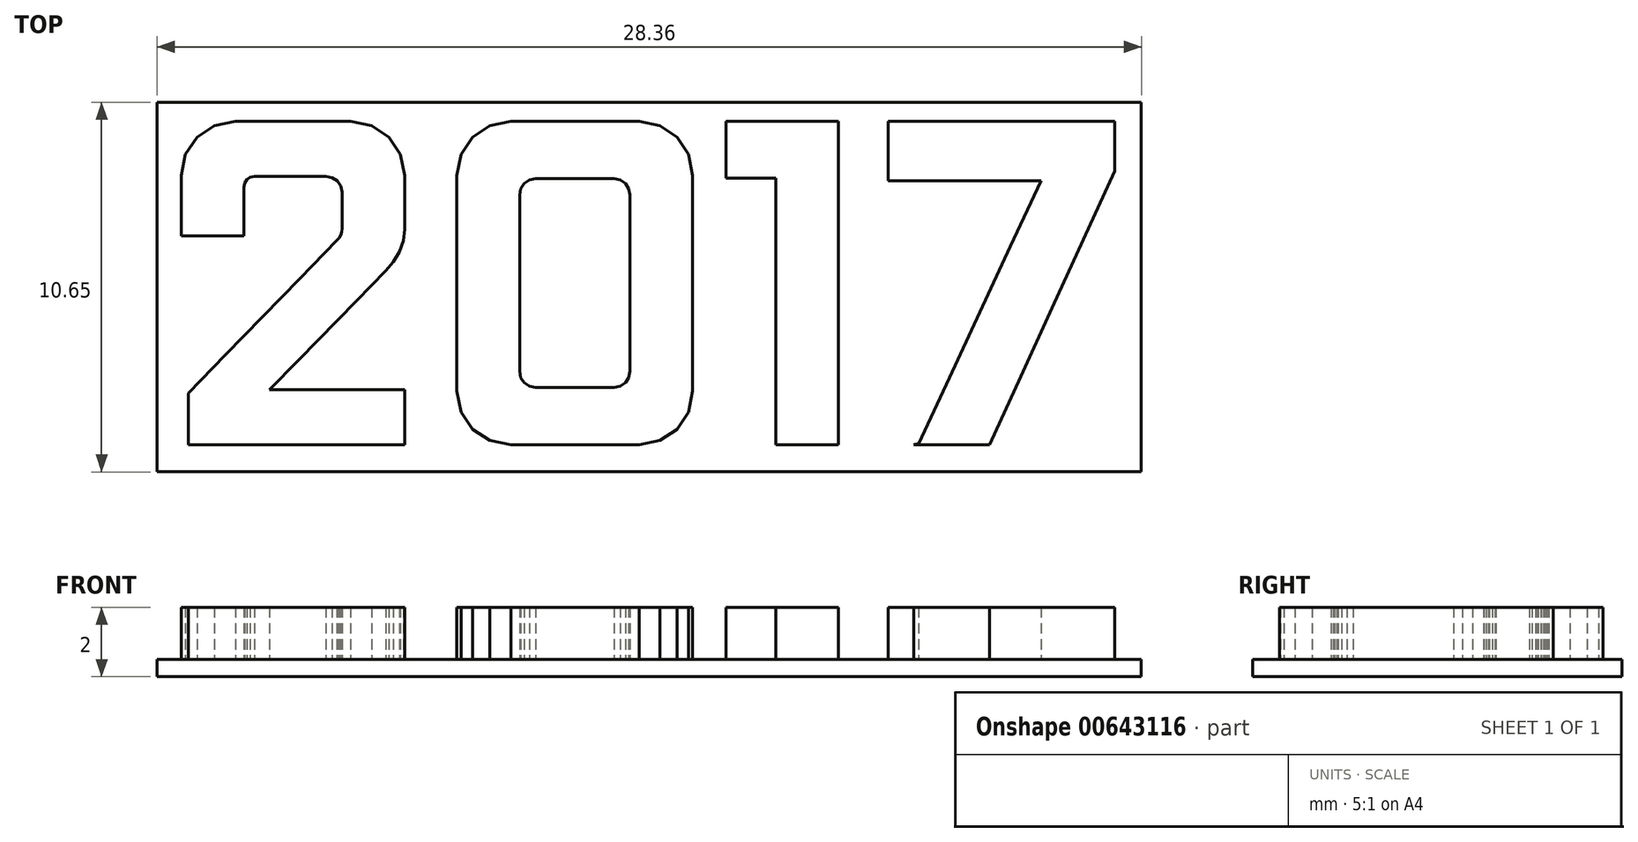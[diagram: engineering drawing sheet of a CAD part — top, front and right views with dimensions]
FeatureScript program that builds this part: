
annotation { "Feature Type Name" : "Feature", "Feature Type Description" : "" }
export const myFeature = defineFeature(function(context is Context, id is Id, definition is map)
    precondition{}
    {
        {
            var Q0;
            Q0=qCreatedBy(makeId("Top.planeOp"),FACE);
            var sketch = newSketch(context, id + "F0", { "sketchPlane" : qUnion([Q0])});
            skLineSegment(sketch, "E0", {"start": v(-11.83, 4.48) * mm, "end": v(-12.44, 4.36) * mm});
            skLineSegment(sketch, "E1", {"start": v(-12.44, 4.36) * mm, "end": v(-12.93, 4.03) * mm});
            skLineSegment(sketch, "E2", {"start": v(-12.93, 4.03) * mm, "end": v(-13.27, 3.53) * mm});
            skLineSegment(sketch, "E3", {"start": v(-13.27, 3.53) * mm, "end": v(-13.39, 2.93) * mm});
            skLineSegment(sketch, "E4", {"start": v(-13.39, 2.93) * mm, "end": v(-13.39, 2.49) * mm});
            skLineSegment(sketch, "E5", {"start": v(-13.39, 2.49) * mm, "end": v(-13.39, 2.05) * mm});
            skLineSegment(sketch, "E6", {"start": v(-13.39, 2.05) * mm, "end": v(-13.39, 1.61) * mm});
            skLineSegment(sketch, "E7", {"start": v(-13.39, 1.61) * mm, "end": v(-13.39, 1.18) * mm});
            skLineSegment(sketch, "E8", {"start": v(-13.39, 1.18) * mm, "end": v(-12.94, 1.18) * mm});
            skLineSegment(sketch, "E9", {"start": v(-12.94, 1.18) * mm, "end": v(-12.49, 1.18) * mm});
            skLineSegment(sketch, "E10", {"start": v(-12.49, 1.18) * mm, "end": v(-12.04, 1.18) * mm});
            skLineSegment(sketch, "E11", {"start": v(-12.04, 1.18) * mm, "end": v(-11.59, 1.18) * mm});
            skLineSegment(sketch, "E12", {"start": v(-11.59, 1.18) * mm, "end": v(-11.59, 1.53) * mm});
            skLineSegment(sketch, "E13", {"start": v(-11.59, 1.53) * mm, "end": v(-11.59, 1.88) * mm});
            skLineSegment(sketch, "E14", {"start": v(-11.59, 1.88) * mm, "end": v(-11.59, 2.23) * mm});
            skLineSegment(sketch, "E15", {"start": v(-11.59, 2.23) * mm, "end": v(-11.59, 2.58) * mm});
            skLineSegment(sketch, "E16", {"start": v(-11.59, 2.58) * mm, "end": v(-11.56, 2.7) * mm});
            skLineSegment(sketch, "E17", {"start": v(-11.56, 2.7) * mm, "end": v(-11.5, 2.8) * mm});
            skLineSegment(sketch, "E18", {"start": v(-11.5, 2.8) * mm, "end": v(-11.4, 2.87) * mm});
            skLineSegment(sketch, "E19", {"start": v(-11.4, 2.87) * mm, "end": v(-11.28, 2.9) * mm});
            skLineSegment(sketch, "E20", {"start": v(-11.28, 2.9) * mm, "end": v(-10.77, 2.9) * mm});
            skLineSegment(sketch, "E21", {"start": v(-10.77, 2.9) * mm, "end": v(-10.25, 2.9) * mm});
            skLineSegment(sketch, "E22", {"start": v(-10.25, 2.9) * mm, "end": v(-9.74, 2.9) * mm});
            skLineSegment(sketch, "E23", {"start": v(-9.74, 2.9) * mm, "end": v(-9.22, 2.9) * mm});
            skLineSegment(sketch, "E24", {"start": v(-9.22, 2.9) * mm, "end": v(-9.04, 2.86) * mm});
            skLineSegment(sketch, "E25", {"start": v(-9.04, 2.86) * mm, "end": v(-8.9, 2.76) * mm});
            skLineSegment(sketch, "E26", {"start": v(-8.9, 2.76) * mm, "end": v(-8.8, 2.62) * mm});
            skLineSegment(sketch, "E27", {"start": v(-8.8, 2.62) * mm, "end": v(-8.76, 2.43) * mm});
            skLineSegment(sketch, "E28", {"start": v(-8.76, 2.43) * mm, "end": v(-8.76, 2.17) * mm});
            skLineSegment(sketch, "E29", {"start": v(-8.76, 2.17) * mm, "end": v(-8.76, 1.91) * mm});
            skLineSegment(sketch, "E30", {"start": v(-8.76, 1.91) * mm, "end": v(-8.76, 1.65) * mm});
            skLineSegment(sketch, "E31", {"start": v(-8.76, 1.65) * mm, "end": v(-8.76, 1.4) * mm});
            skLineSegment(sketch, "E32", {"start": v(-8.76, 1.4) * mm, "end": v(-8.77, 1.3) * mm});
            skLineSegment(sketch, "E33", {"start": v(-8.77, 1.3) * mm, "end": v(-8.8, 1.2) * mm});
            skLineSegment(sketch, "E34", {"start": v(-8.8, 1.2) * mm, "end": v(-8.84, 1.12) * mm});
            skLineSegment(sketch, "E35", {"start": v(-8.84, 1.12) * mm, "end": v(-8.9, 1.05) * mm});
            skLineSegment(sketch, "E36", {"start": v(-8.9, 1.05) * mm, "end": v(-9.98, -0.05) * mm});
            skLineSegment(sketch, "E37", {"start": v(-9.98, -0.05) * mm, "end": v(-11.05, -1.15) * mm});
            skLineSegment(sketch, "E38", {"start": v(-11.05, -1.15) * mm, "end": v(-12.11, -2.25) * mm});
            skLineSegment(sketch, "E39", {"start": v(-12.11, -2.25) * mm, "end": v(-13.18, -3.35) * mm});
            skLineSegment(sketch, "E40", {"start": v(-13.18, -3.35) * mm, "end": v(-13.18, -3.72) * mm});
            skLineSegment(sketch, "E41", {"start": v(-13.18, -3.72) * mm, "end": v(-13.18, -4.1) * mm});
            skLineSegment(sketch, "E42", {"start": v(-13.18, -4.1) * mm, "end": v(-13.18, -4.47) * mm});
            skLineSegment(sketch, "E43", {"start": v(-13.18, -4.47) * mm, "end": v(-13.18, -4.84) * mm});
            skLineSegment(sketch, "E44", {"start": v(-13.18, -4.84) * mm, "end": v(-11.63, -4.84) * mm});
            skLineSegment(sketch, "E45", {"start": v(-11.63, -4.84) * mm, "end": v(-10.07, -4.84) * mm});
            skLineSegment(sketch, "E46", {"start": v(-10.07, -4.84) * mm, "end": v(-8.5, -4.84) * mm});
            skLineSegment(sketch, "E47", {"start": v(-8.5, -4.84) * mm, "end": v(-6.95, -4.84) * mm});
            skLineSegment(sketch, "E48", {"start": v(-6.95, -4.84) * mm, "end": v(-6.95, -4.44) * mm});
            skLineSegment(sketch, "E49", {"start": v(-6.95, -4.44) * mm, "end": v(-6.95, -4.05) * mm});
            skLineSegment(sketch, "E50", {"start": v(-6.95, -4.05) * mm, "end": v(-6.95, -3.65) * mm});
            skLineSegment(sketch, "E51", {"start": v(-6.95, -3.65) * mm, "end": v(-6.95, -3.25) * mm});
            skLineSegment(sketch, "E52", {"start": v(-6.95, -3.25) * mm, "end": v(-7.93, -3.25) * mm});
            skLineSegment(sketch, "E53", {"start": v(-7.93, -3.25) * mm, "end": v(-8.9, -3.25) * mm});
            skLineSegment(sketch, "E54", {"start": v(-8.9, -3.25) * mm, "end": v(-9.87, -3.25) * mm});
            skLineSegment(sketch, "E55", {"start": v(-9.87, -3.25) * mm, "end": v(-10.85, -3.25) * mm});
            skLineSegment(sketch, "E56", {"start": v(-10.85, -3.25) * mm, "end": v(-10, -2.4) * mm});
            skLineSegment(sketch, "E57", {"start": v(-10, -2.4) * mm, "end": v(-9.17, -1.54) * mm});
            skLineSegment(sketch, "E58", {"start": v(-9.17, -1.54) * mm, "end": v(-8.34, -0.68) * mm});
            skLineSegment(sketch, "E59", {"start": v(-8.34, -0.68) * mm, "end": v(-7.5, 0.18) * mm});
            skLineSegment(sketch, "E60", {"start": v(-7.5, 0.18) * mm, "end": v(-7.27, 0.43) * mm});
            skLineSegment(sketch, "E61", {"start": v(-7.27, 0.43) * mm, "end": v(-7.1, 0.72) * mm});
            skLineSegment(sketch, "E62", {"start": v(-7.1, 0.72) * mm, "end": v(-7, 1.04) * mm});
            skLineSegment(sketch, "E63", {"start": v(-7, 1.04) * mm, "end": v(-6.95, 1.37) * mm});
            skLineSegment(sketch, "E64", {"start": v(-6.95, 1.37) * mm, "end": v(-6.95, 1.76) * mm});
            skLineSegment(sketch, "E65", {"start": v(-6.95, 1.76) * mm, "end": v(-6.95, 2.15) * mm});
            skLineSegment(sketch, "E66", {"start": v(-6.95, 2.15) * mm, "end": v(-6.95, 2.54) * mm});
            skLineSegment(sketch, "E67", {"start": v(-6.95, 2.54) * mm, "end": v(-6.95, 2.93) * mm});
            skLineSegment(sketch, "E68", {"start": v(-6.95, 2.93) * mm, "end": v(-7.07, 3.53) * mm});
            skLineSegment(sketch, "E69", {"start": v(-7.07, 3.53) * mm, "end": v(-7.4, 4.03) * mm});
            skLineSegment(sketch, "E70", {"start": v(-7.4, 4.03) * mm, "end": v(-7.9, 4.36) * mm});
            skLineSegment(sketch, "E71", {"start": v(-7.9, 4.36) * mm, "end": v(-8.5, 4.48) * mm});
            skLineSegment(sketch, "E72", {"start": v(-8.5, 4.48) * mm, "end": v(-9.34, 4.48) * mm});
            skLineSegment(sketch, "E73", {"start": v(-9.34, 4.48) * mm, "end": v(-10.17, 4.48) * mm});
            skLineSegment(sketch, "E74", {"start": v(-10.17, 4.48) * mm, "end": v(-11, 4.48) * mm});
            skLineSegment(sketch, "E75", {"start": v(-11, 4.48) * mm, "end": v(-11.83, 4.48) * mm});
            skLineSegment(sketch, "E76", {"start": v(-3.64, -2.72) * mm, "end": v(-3.64, -1.45) * mm});
            skLineSegment(sketch, "E77", {"start": v(-3.64, -1.45) * mm, "end": v(-3.64, -0.18) * mm});
            skLineSegment(sketch, "E78", {"start": v(-3.64, -0.18) * mm, "end": v(-3.64, 1.1) * mm});
            skLineSegment(sketch, "E79", {"start": v(-3.64, 1.1) * mm, "end": v(-3.64, 2.37) * mm});
            skLineSegment(sketch, "E80", {"start": v(-3.64, 2.37) * mm, "end": v(-3.6, 2.54) * mm});
            skLineSegment(sketch, "E81", {"start": v(-3.6, 2.54) * mm, "end": v(-3.5, 2.69) * mm});
            skLineSegment(sketch, "E82", {"start": v(-3.5, 2.69) * mm, "end": v(-3.35, 2.8) * mm});
            skLineSegment(sketch, "E83", {"start": v(-3.35, 2.8) * mm, "end": v(-3.17, 2.83) * mm});
            skLineSegment(sketch, "E84", {"start": v(-3.17, 2.83) * mm, "end": v(-2.61, 2.83) * mm});
            skLineSegment(sketch, "E85", {"start": v(-2.61, 2.83) * mm, "end": v(-2.05, 2.83) * mm});
            skLineSegment(sketch, "E86", {"start": v(-2.05, 2.83) * mm, "end": v(-1.48, 2.83) * mm});
            skLineSegment(sketch, "E87", {"start": v(-1.48, 2.83) * mm, "end": v(-0.92, 2.83) * mm});
            skLineSegment(sketch, "E88", {"start": v(-0.92, 2.83) * mm, "end": v(-0.74, 2.8) * mm});
            skLineSegment(sketch, "E89", {"start": v(-0.74, 2.8) * mm, "end": v(-0.59, 2.69) * mm});
            skLineSegment(sketch, "E90", {"start": v(-0.59, 2.69) * mm, "end": v(-0.5, 2.54) * mm});
            skLineSegment(sketch, "E91", {"start": v(-0.5, 2.54) * mm, "end": v(-0.45, 2.37) * mm});
            skLineSegment(sketch, "E92", {"start": v(-0.45, 2.37) * mm, "end": v(-0.45, 1.1) * mm});
            skLineSegment(sketch, "E93", {"start": v(-0.45, 1.1) * mm, "end": v(-0.45, -0.18) * mm});
            skLineSegment(sketch, "E94", {"start": v(-0.45, -0.18) * mm, "end": v(-0.45, -1.45) * mm});
            skLineSegment(sketch, "E95", {"start": v(-0.45, -1.45) * mm, "end": v(-0.45, -2.72) * mm});
            skLineSegment(sketch, "E96", {"start": v(-0.45, -2.72) * mm, "end": v(-0.5, -2.9) * mm});
            skLineSegment(sketch, "E97", {"start": v(-0.5, -2.9) * mm, "end": v(-0.59, -3.05) * mm});
            skLineSegment(sketch, "E98", {"start": v(-0.59, -3.05) * mm, "end": v(-0.74, -3.15) * mm});
            skLineSegment(sketch, "E99", {"start": v(-0.74, -3.15) * mm, "end": v(-0.92, -3.18) * mm});
            skLineSegment(sketch, "E100", {"start": v(-0.92, -3.18) * mm, "end": v(-1.48, -3.18) * mm});
            skLineSegment(sketch, "E101", {"start": v(-1.48, -3.18) * mm, "end": v(-2.05, -3.18) * mm});
            skLineSegment(sketch, "E102", {"start": v(-2.05, -3.18) * mm, "end": v(-2.61, -3.18) * mm});
            skLineSegment(sketch, "E103", {"start": v(-2.61, -3.18) * mm, "end": v(-3.17, -3.18) * mm});
            skLineSegment(sketch, "E104", {"start": v(-3.17, -3.18) * mm, "end": v(-3.35, -3.15) * mm});
            skLineSegment(sketch, "E105", {"start": v(-3.35, -3.15) * mm, "end": v(-3.5, -3.05) * mm});
            skLineSegment(sketch, "E106", {"start": v(-3.5, -3.05) * mm, "end": v(-3.6, -2.9) * mm});
            skLineSegment(sketch, "E107", {"start": v(-3.6, -2.9) * mm, "end": v(-3.64, -2.72) * mm});
            skLineSegment(sketch, "E108", {"start": v(-3.89, 4.48) * mm, "end": v(-4.5, 4.36) * mm});
            skLineSegment(sketch, "E109", {"start": v(-4.5, 4.36) * mm, "end": v(-4.99, 4.03) * mm});
            skLineSegment(sketch, "E110", {"start": v(-4.99, 4.03) * mm, "end": v(-5.32, 3.53) * mm});
            skLineSegment(sketch, "E111", {"start": v(-5.32, 3.53) * mm, "end": v(-5.44, 2.93) * mm});
            skLineSegment(sketch, "E112", {"start": v(-5.44, 2.93) * mm, "end": v(-5.44, 1.37) * mm});
            skLineSegment(sketch, "E113", {"start": v(-5.44, 1.37) * mm, "end": v(-5.44, -0.18) * mm});
            skLineSegment(sketch, "E114", {"start": v(-5.44, -0.18) * mm, "end": v(-5.44, -1.74) * mm});
            skLineSegment(sketch, "E115", {"start": v(-5.44, -1.74) * mm, "end": v(-5.44, -3.3) * mm});
            skLineSegment(sketch, "E116", {"start": v(-5.44, -3.3) * mm, "end": v(-5.32, -3.9) * mm});
            skLineSegment(sketch, "E117", {"start": v(-5.32, -3.9) * mm, "end": v(-4.99, -4.39) * mm});
            skLineSegment(sketch, "E118", {"start": v(-4.99, -4.39) * mm, "end": v(-4.5, -4.72) * mm});
            skLineSegment(sketch, "E119", {"start": v(-4.5, -4.72) * mm, "end": v(-3.89, -4.84) * mm});
            skLineSegment(sketch, "E120", {"start": v(-3.89, -4.84) * mm, "end": v(-2.96, -4.84) * mm});
            skLineSegment(sketch, "E121", {"start": v(-2.96, -4.84) * mm, "end": v(-2.04, -4.84) * mm});
            skLineSegment(sketch, "E122", {"start": v(-2.04, -4.84) * mm, "end": v(-1.12, -4.84) * mm});
            skLineSegment(sketch, "E123", {"start": v(-1.12, -4.84) * mm, "end": v(-0.2, -4.84) * mm});
            skLineSegment(sketch, "E124", {"start": v(-0.2, -4.84) * mm, "end": v(0.4, -4.72) * mm});
            skLineSegment(sketch, "E125", {"start": v(0.4, -4.72) * mm, "end": v(0.9, -4.39) * mm});
            skLineSegment(sketch, "E126", {"start": v(0.9, -4.39) * mm, "end": v(1.23, -3.9) * mm});
            skLineSegment(sketch, "E127", {"start": v(1.23, -3.9) * mm, "end": v(1.35, -3.3) * mm});
            skLineSegment(sketch, "E128", {"start": v(1.35, -3.3) * mm, "end": v(1.35, -1.74) * mm});
            skLineSegment(sketch, "E129", {"start": v(1.35, -1.74) * mm, "end": v(1.35, -0.18) * mm});
            skLineSegment(sketch, "E130", {"start": v(1.35, -0.18) * mm, "end": v(1.35, 1.37) * mm});
            skLineSegment(sketch, "E131", {"start": v(1.35, 1.37) * mm, "end": v(1.35, 2.93) * mm});
            skLineSegment(sketch, "E132", {"start": v(1.35, 2.93) * mm, "end": v(1.23, 3.53) * mm});
            skLineSegment(sketch, "E133", {"start": v(1.23, 3.53) * mm, "end": v(0.9, 4.03) * mm});
            skLineSegment(sketch, "E134", {"start": v(0.9, 4.03) * mm, "end": v(0.4, 4.36) * mm});
            skLineSegment(sketch, "E135", {"start": v(0.4, 4.36) * mm, "end": v(-0.2, 4.48) * mm});
            skLineSegment(sketch, "E136", {"start": v(-0.2, 4.48) * mm, "end": v(-1.12, 4.48) * mm});
            skLineSegment(sketch, "E137", {"start": v(-1.12, 4.48) * mm, "end": v(-2.04, 4.48) * mm});
            skLineSegment(sketch, "E138", {"start": v(-2.04, 4.48) * mm, "end": v(-2.96, 4.48) * mm});
            skLineSegment(sketch, "E139", {"start": v(-2.96, 4.48) * mm, "end": v(-3.89, 4.48) * mm});
            skLineSegment(sketch, "E140", {"start": v(2.31, 4.48) * mm, "end": v(2.31, 4.07) * mm});
            skLineSegment(sketch, "E141", {"start": v(2.31, 4.07) * mm, "end": v(2.31, 3.66) * mm});
            skLineSegment(sketch, "E142", {"start": v(2.31, 3.66) * mm, "end": v(2.31, 3.25) * mm});
            skLineSegment(sketch, "E143", {"start": v(2.31, 3.25) * mm, "end": v(2.31, 2.84) * mm});
            skLineSegment(sketch, "E144", {"start": v(2.31, 2.84) * mm, "end": v(2.67, 2.84) * mm});
            skLineSegment(sketch, "E145", {"start": v(2.67, 2.84) * mm, "end": v(3.03, 2.84) * mm});
            skLineSegment(sketch, "E146", {"start": v(3.03, 2.84) * mm, "end": v(3.39, 2.84) * mm});
            skLineSegment(sketch, "E147", {"start": v(3.39, 2.84) * mm, "end": v(3.75, 2.84) * mm});
            skLineSegment(sketch, "E148", {"start": v(3.75, 2.84) * mm, "end": v(3.75, 0.92) * mm});
            skLineSegment(sketch, "E149", {"start": v(3.75, 0.92) * mm, "end": v(3.75, -1) * mm});
            skLineSegment(sketch, "E150", {"start": v(3.75, -1) * mm, "end": v(3.75, -2.92) * mm});
            skLineSegment(sketch, "E151", {"start": v(3.75, -2.92) * mm, "end": v(3.75, -4.84) * mm});
            skLineSegment(sketch, "E152", {"start": v(3.75, -4.84) * mm, "end": v(4.2, -4.84) * mm});
            skLineSegment(sketch, "E153", {"start": v(4.2, -4.84) * mm, "end": v(4.65, -4.84) * mm});
            skLineSegment(sketch, "E154", {"start": v(4.65, -4.84) * mm, "end": v(5.1, -4.84) * mm});
            skLineSegment(sketch, "E155", {"start": v(5.1, -4.84) * mm, "end": v(5.55, -4.84) * mm});
            skLineSegment(sketch, "E156", {"start": v(5.55, -4.84) * mm, "end": v(5.55, -2.5) * mm});
            skLineSegment(sketch, "E157", {"start": v(5.55, -2.5) * mm, "end": v(5.55, -0.18) * mm});
            skLineSegment(sketch, "E158", {"start": v(5.55, -0.18) * mm, "end": v(5.55, 2.15) * mm});
            skLineSegment(sketch, "E159", {"start": v(5.55, 2.15) * mm, "end": v(5.55, 4.48) * mm});
            skLineSegment(sketch, "E160", {"start": v(5.55, 4.48) * mm, "end": v(4.74, 4.48) * mm});
            skLineSegment(sketch, "E161", {"start": v(4.74, 4.48) * mm, "end": v(3.93, 4.48) * mm});
            skLineSegment(sketch, "E162", {"start": v(3.93, 4.48) * mm, "end": v(3.12, 4.48) * mm});
            skLineSegment(sketch, "E163", {"start": v(3.12, 4.48) * mm, "end": v(2.31, 4.48) * mm});
            skLineSegment(sketch, "E164", {"start": v(6.99, 4.48) * mm, "end": v(6.99, 4.06) * mm});
            skLineSegment(sketch, "E165", {"start": v(6.99, 4.06) * mm, "end": v(6.99, 3.63) * mm});
            skLineSegment(sketch, "E166", {"start": v(6.99, 3.63) * mm, "end": v(6.99, 3.2) * mm});
            skLineSegment(sketch, "E167", {"start": v(6.99, 3.2) * mm, "end": v(6.99, 2.77) * mm});
            skLineSegment(sketch, "E168", {"start": v(6.99, 2.77) * mm, "end": v(8.09, 2.77) * mm});
            skLineSegment(sketch, "E169", {"start": v(8.09, 2.77) * mm, "end": v(9.19, 2.77) * mm});
            skLineSegment(sketch, "E170", {"start": v(9.19, 2.77) * mm, "end": v(10.29, 2.77) * mm});
            skLineSegment(sketch, "E171", {"start": v(10.29, 2.77) * mm, "end": v(11.39, 2.77) * mm});
            skLineSegment(sketch, "E172", {"start": v(11.39, 2.77) * mm, "end": v(10.5, 0.88) * mm});
            skLineSegment(sketch, "E173", {"start": v(10.5, 0.88) * mm, "end": v(9.63, -1.02) * mm});
            skLineSegment(sketch, "E174", {"start": v(9.63, -1.02) * mm, "end": v(8.74, -2.91) * mm});
            skLineSegment(sketch, "E175", {"start": v(8.74, -2.91) * mm, "end": v(7.86, -4.81) * mm});
            skLineSegment(sketch, "E176", {"start": v(7.86, -4.81) * mm, "end": v(7.83, -4.82) * mm});
            skLineSegment(sketch, "E177", {"start": v(7.83, -4.82) * mm, "end": v(7.8, -4.82) * mm});
            skLineSegment(sketch, "E178", {"start": v(7.8, -4.82) * mm, "end": v(7.76, -4.83) * mm});
            skLineSegment(sketch, "E179", {"start": v(7.76, -4.83) * mm, "end": v(7.73, -4.84) * mm});
            skLineSegment(sketch, "E180", {"start": v(7.73, -4.84) * mm, "end": v(8.27, -4.84) * mm});
            skLineSegment(sketch, "E181", {"start": v(8.27, -4.84) * mm, "end": v(8.81, -4.84) * mm});
            skLineSegment(sketch, "E182", {"start": v(8.81, -4.84) * mm, "end": v(9.36, -4.84) * mm});
            skLineSegment(sketch, "E183", {"start": v(9.36, -4.84) * mm, "end": v(9.9, -4.84) * mm});
            skLineSegment(sketch, "E184", {"start": v(9.9, -4.84) * mm, "end": v(10.8, -2.87) * mm});
            skLineSegment(sketch, "E185", {"start": v(10.8, -2.87) * mm, "end": v(11.7, -0.9) * mm});
            skLineSegment(sketch, "E186", {"start": v(11.7, -0.9) * mm, "end": v(12.6, 1.08) * mm});
            skLineSegment(sketch, "E187", {"start": v(12.6, 1.08) * mm, "end": v(13.5, 3.05) * mm});
            skLineSegment(sketch, "E188", {"start": v(13.5, 3.05) * mm, "end": v(13.5, 3.4) * mm});
            skLineSegment(sketch, "E189", {"start": v(13.5, 3.4) * mm, "end": v(13.5, 3.77) * mm});
            skLineSegment(sketch, "E190", {"start": v(13.5, 3.77) * mm, "end": v(13.5, 4.13) * mm});
            skLineSegment(sketch, "E191", {"start": v(13.5, 4.13) * mm, "end": v(13.5, 4.48) * mm});
            skLineSegment(sketch, "E192", {"start": v(13.5, 4.48) * mm, "end": v(11.88, 4.48) * mm});
            skLineSegment(sketch, "E193", {"start": v(11.88, 4.48) * mm, "end": v(10.25, 4.48) * mm});
            skLineSegment(sketch, "E194", {"start": v(10.25, 4.48) * mm, "end": v(8.62, 4.48) * mm});
            skLineSegment(sketch, "E195", {"start": v(8.62, 4.48) * mm, "end": v(6.99, 4.48) * mm});
            skLineSegment(sketch, "E196.bottom", {"start": v(-14.08, 5.03) * mm, "end": v(14.28, 5.03) * mm});
            skLineSegment(sketch, "E196.top", {"start": v(-14.08, -5.62) * mm, "end": v(14.28, -5.62) * mm});
            skLineSegment(sketch, "E196.left", {"start": v(-14.08, 5.03) * mm, "end": v(-14.08, -5.62) * mm});
            skLineSegment(sketch, "E196.right", {"start": v(14.28, 5.03) * mm, "end": v(14.28, -5.62) * mm});
            skSolve(sketch);
        }
        {
            var Q0;
            Q0=makeQuery(id+"F0.imprint","IMPRINT",FACE,{"disambiguationData":[TD([[makeQuery(id+"F0.imprint","IMPRINT",EDGE,{"derivedFrom":sQuery(id+"F0.wireOp",EDGE,"E0")}),-1.0]])]});
            var Q1;
            Q1=makeQuery(id+"F0.imprint","IMPRINT",FACE,{"disambiguationData":[TD([[makeQuery(id+"F0.imprint","IMPRINT",EDGE,{"derivedFrom":sQuery(id+"F0.wireOp",EDGE,"E76")}),-1.0]])]});
            extrude(context, id + "F1", {"entities" : qUnion([Q0, Q1]), "depth" : 0.5 * mm, "offsetDistance" : 25 * mm});
        }
        {
            var Q0;
            Q0=makeQuery(id+"F0.imprint","IMPRINT",FACE,{"disambiguationData":[TD([[makeQuery(id+"F0.imprint","IMPRINT",EDGE,{"derivedFrom":sQuery(id+"F0.wireOp",EDGE,"E0")}),1.0]])]});
            var Q1;
            Q1=makeQuery(id+"F0.imprint","IMPRINT",FACE,{"disambiguationData":[TD([[makeQuery(id+"F0.imprint","IMPRINT",EDGE,{"derivedFrom":sQuery(id+"F0.wireOp",EDGE,"E76")}),1.0]])]});
            var Q2;
            Q2=makeQuery(id+"F0.imprint","IMPRINT",FACE,{"disambiguationData":[TD([[makeQuery(id+"F0.imprint","IMPRINT",EDGE,{"derivedFrom":sQuery(id+"F0.wireOp",EDGE,"E140")}),1.0]])]});
            var Q3;
            Q3=makeQuery(id+"F0.imprint","IMPRINT",FACE,{"disambiguationData":[TD([[makeQuery(id+"F0.imprint","IMPRINT",EDGE,{"derivedFrom":sQuery(id+"F0.wireOp",EDGE,"E164")}),1.0]])]});
            extrude(context, id + "F2", {"entities" : qUnion([Q0, Q1, Q2, Q3]), "operationType" : NewBodyOperationType.ADD, "depth" : 2 * mm, "offsetDistance" : 25 * mm});
        }
    });
